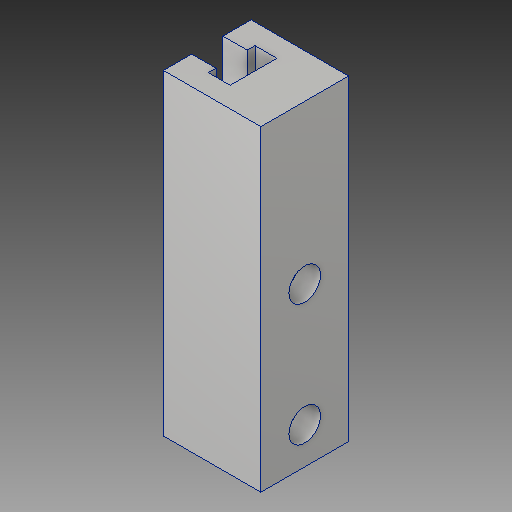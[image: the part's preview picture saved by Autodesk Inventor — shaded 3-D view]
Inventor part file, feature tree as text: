
AUTODESK INVENTOR PART (.ipt)
format: ipt  version: 2019 (Build 230136000, 136)  size: 145,920 bytes
history: native  units: mm
features: extrude x4, sketch x3
ambient origin geometry x8: Origin, YZ Plane, XZ Plane, XY Plane, X Axis, Y Axis, Z Axis, Center Point
bodies: Solid1 (feature_tree)
feature tree (7):
  extrude  "Extrusion1"  Depth=20.0mm
  sketch  "Sketch2"  dims[d2=65.0mm d3=0.0mm d4=6.5mm]
  extrude  "Extrusion2"  Depth=65.0mm
  extrude  "Extrusion3"  Depth=10.0mm
  extrude  "Extrusion4"  Depth=10.0mm
  sketch  "Sketch1"  dims[d0=18.0mm d1=20.0mm]
  sketch  "Sketch4"  dims[d5=6.5mm d8=11.0mm d9=11.0mm d10=50.0mm d11=0.0mm d12=15.5mm d13=0.0mm d28=6.4mm d29=4.5mm d30=9.6mm d31=5.0mm d32=10.0mm d33=0.0mm d34=25.0mm d15=1.0mm d16=1.0mm]
